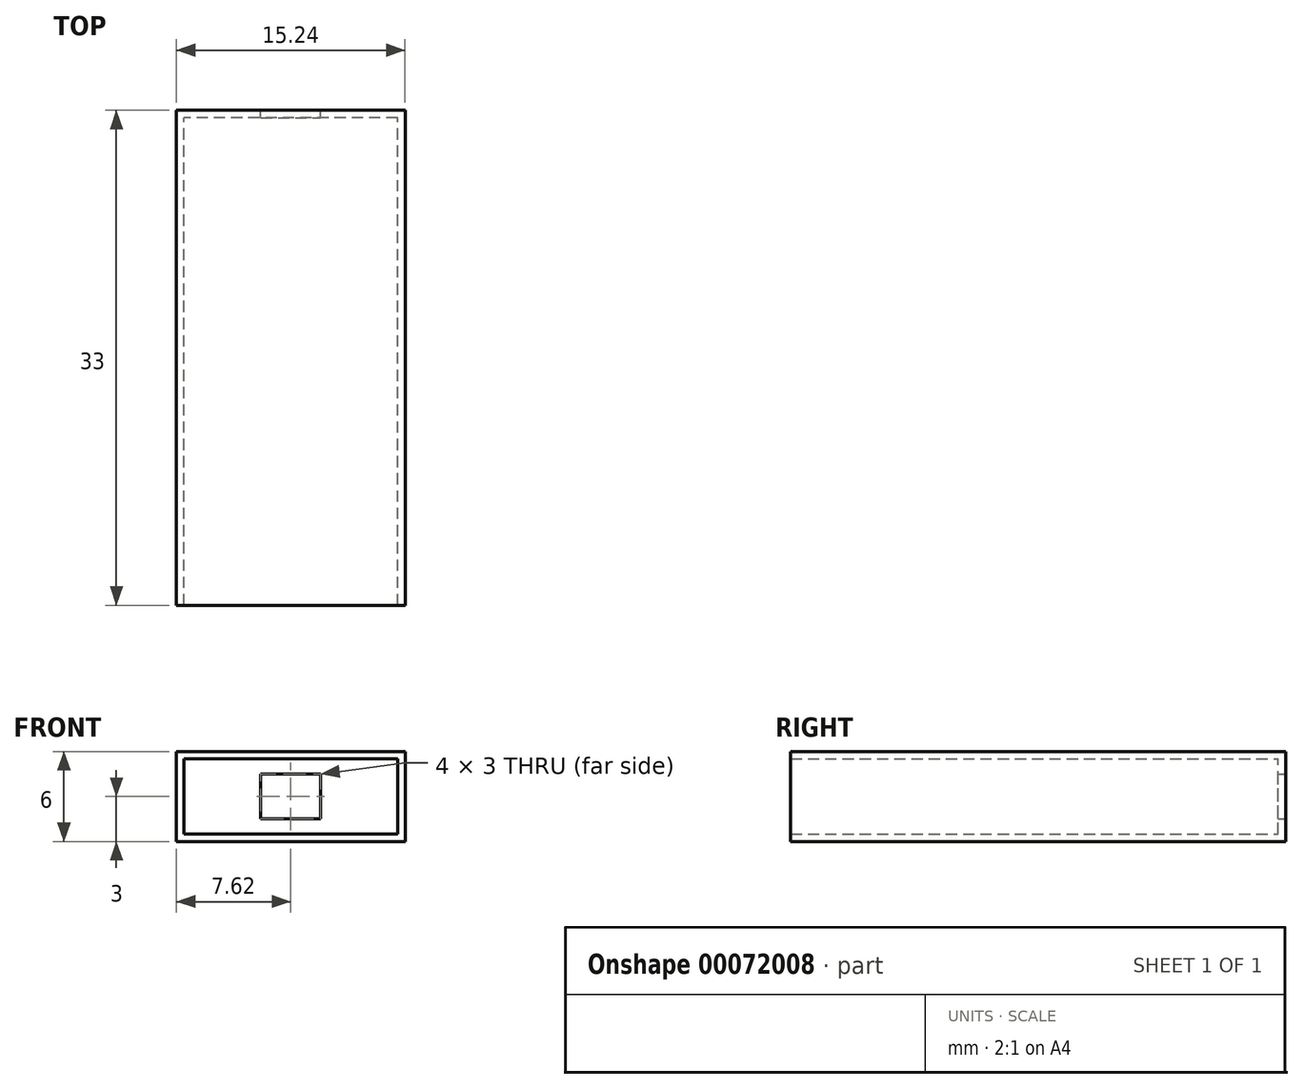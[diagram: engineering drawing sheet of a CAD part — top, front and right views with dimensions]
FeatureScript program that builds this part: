
annotation { "Feature Type Name" : "Feature", "Feature Type Description" : "" }
export const myFeature = defineFeature(function(context is Context, id is Id, definition is map)
    precondition{}
    {
        {
            var Q0;
            Q0=qCreatedBy(makeId("Front.planeOp"),FACE);
            var sketch = newSketch(context, id + "F0", { "sketchPlane" : qUnion([Q0])});
            skLineSegment(sketch, "E0.rect.bottom", {"start": v(7.62, -3) * mm, "end": v(-7.62, -3) * mm});
            skLineSegment(sketch, "E0.rect.top", {"start": v(7.62, 3) * mm, "end": v(-7.63, 3) * mm});
            skLineSegment(sketch, "E0.rect.left", {"start": v(7.62, -3) * mm, "end": v(7.62, 3) * mm});
            skLineSegment(sketch, "E0.rect.right", {"start": v(-7.62, -3) * mm, "end": v(-7.63, 3) * mm});
            skPoint(sketch, "E0.rect.middle", {"position": v(0, 0) * mm});
            skLineSegment(sketch, "E1.0", {"start": v(7.12, 2.5) * mm, "end": v(-7.13, 2.5) * mm});
            skLineSegment(sketch, "E1.1", {"start": v(7.12, -2.5) * mm, "end": v(7.12, 2.5) * mm});
            skLineSegment(sketch, "E1.2", {"start": v(7.13, -2.5) * mm, "end": v(-7.12, -2.5) * mm});
            skLineSegment(sketch, "E1.3", {"start": v(-7.12, -2.5) * mm, "end": v(-7.13, 2.5) * mm});
            skSolve(sketch);
        }
        {
            var Q0;
            Q0=makeQuery(id+"F0.imprint","IMPRINT",FACE,{"disambiguationData":[TD([[makeQuery(id+"F0.imprint","IMPRINT",EDGE,{"derivedFrom":sQuery(id+"F0.wireOp",EDGE,"E0.rect.bottom")}),-1.0]])]});
            extrude(context, id + "F1", {"entities" : qUnion([Q0]), "depth" : 32.5 * mm});
        }
        {
            var Q0;
            Q0=makeQuery(id+"F1.opExtrude","CAP_FACE",FACE,{"disambiguationData":[OSD([sQuery(id+"F0.wireOp",EDGE,"E0.rect.bottom"),sQuery(id+"F0.wireOp",EDGE,"E0.rect.top"),sQuery(id+"F0.wireOp",EDGE,"E0.rect.left"),sQuery(id+"F0.wireOp",EDGE,"E0.rect.right"),sQuery(id+"F0.wireOp",EDGE,"E1.0"),sQuery(id+"F0.wireOp",EDGE,"E1.1"),sQuery(id+"F0.wireOp",EDGE,"E1.2"),sQuery(id+"F0.wireOp",EDGE,"E1.3")])],"isStart":true});
            var sketch = newSketch(context, id + "F2", { "sketchPlane" : qUnion([Q0])});
            skLineSegment(sketch, "E2.rect.bottom", {"start": v(-7.62, 3) * mm, "end": v(7.62, 3) * mm});
            skLineSegment(sketch, "E2.rect.top", {"start": v(-7.62, -3) * mm, "end": v(7.62, -3) * mm});
            skLineSegment(sketch, "E2.rect.left", {"start": v(-7.62, 3) * mm, "end": v(-7.62, -3) * mm});
            skLineSegment(sketch, "E2.rect.right", {"start": v(7.62, 3) * mm, "end": v(7.62, -3) * mm});
            skPoint(sketch, "E2.rect.middle", {"position": v(0, 0) * mm});
            skSolve(sketch);
        }
        {
            var Q0;
            Q0 = qSketchRegion(id + "F2", true);
            extrude(context, id + "F3", {"entities" : qUnion([Q0]), "operationType" : NewBodyOperationType.ADD, "depth" : .5 * mm});
        }
        {
            var Q0;
            Q0=makeQuery(id+"F3.opExtrude","CAP_FACE",FACE,{"disambiguationData":[OSD([sQuery(id+"F2.wireOp",EDGE,"E2.rect.bottom"),sQuery(id+"F2.wireOp",EDGE,"E2.rect.top"),sQuery(id+"F2.wireOp",EDGE,"E2.rect.left"),sQuery(id+"F2.wireOp",EDGE,"E2.rect.right")])],"isStart":false});
            var sketch = newSketch(context, id + "F4", { "sketchPlane" : qUnion([Q0])});
            skLineSegment(sketch, "E3.rect.bottom", {"start": v(2, -1.5) * mm, "end": v(-2, -1.5) * mm});
            skLineSegment(sketch, "E3.rect.top", {"start": v(2, 1.5) * mm, "end": v(-2, 1.5) * mm});
            skLineSegment(sketch, "E3.rect.left", {"start": v(2, -1.5) * mm, "end": v(2, 1.5) * mm});
            skLineSegment(sketch, "E3.rect.right", {"start": v(-2, -1.5) * mm, "end": v(-2, 1.5) * mm});
            skPoint(sketch, "E3.rect.middle", {"position": v(0, 0) * mm});
            skSolve(sketch);
        }
        {
            var Q0;
            Q0 = qSketchRegion(id + "F4", true);
            extrude(context, id + "F5", {"entities" : qUnion([Q0]), "operationType" : NewBodyOperationType.REMOVE, "endBound" : BoundingType.THROUGH_ALL, "oppositeDirection" : true, "depth" : 25 * mm});
        }
    });
